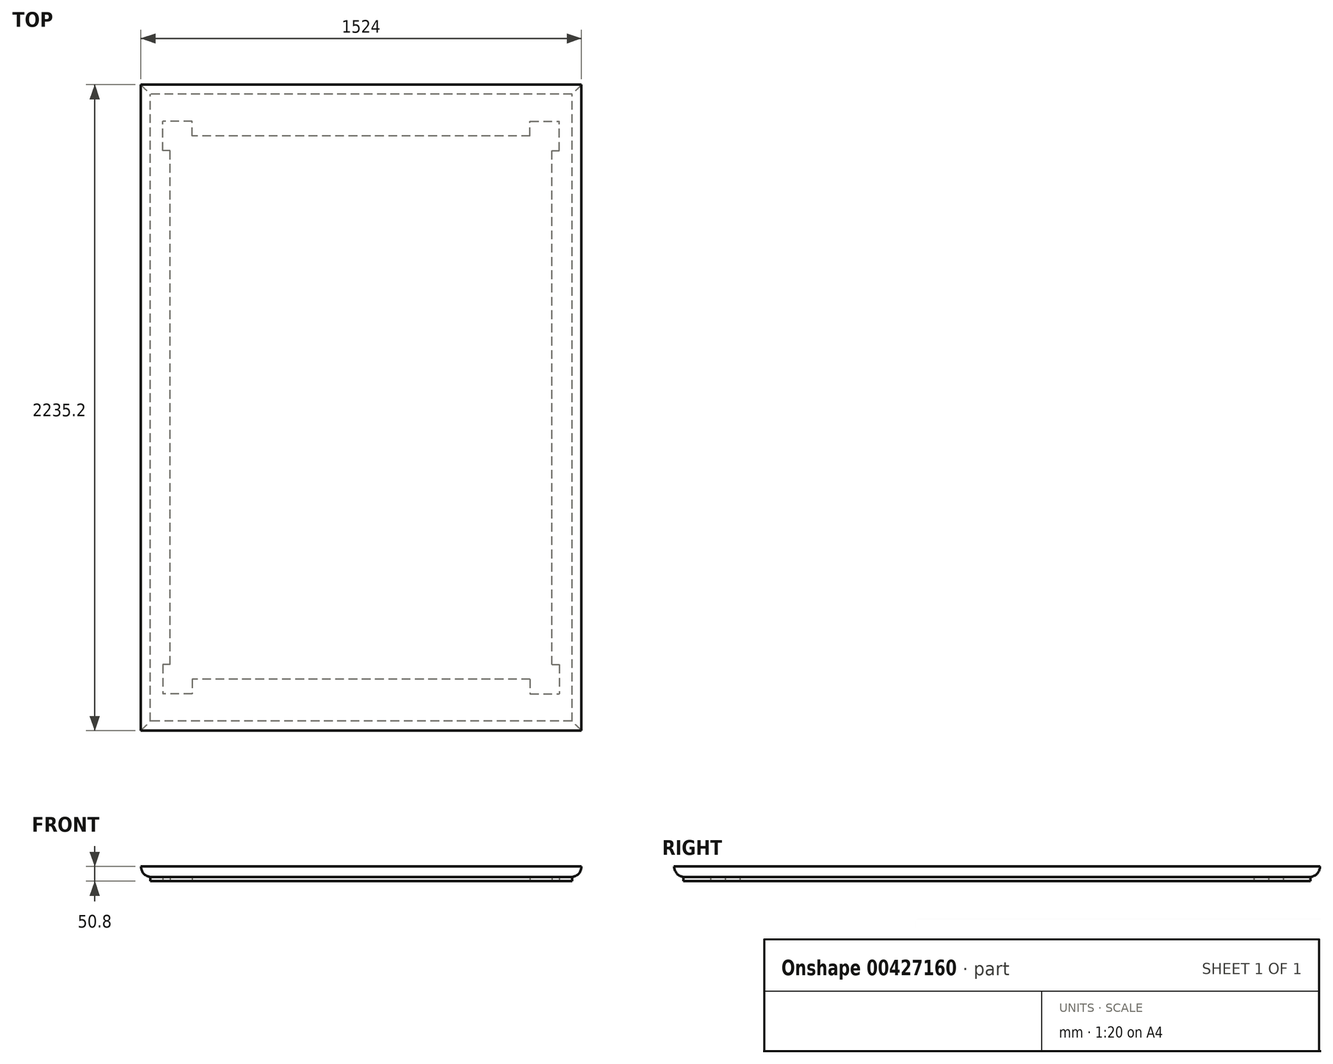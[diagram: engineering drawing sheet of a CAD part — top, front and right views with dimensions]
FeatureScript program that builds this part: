
annotation { "Feature Type Name" : "Feature", "Feature Type Description" : "" }
export const myFeature = defineFeature(function(context is Context, id is Id, definition is map)
    precondition{}
    {
        {
            var Q0;
            Q0=qCreatedBy(makeId("Top.planeOp"),FACE);
            var sketch = newSketch(context, id + "F0", { "sketchPlane" : qUnion([Q0])});
            skLineSegment(sketch, "E0.bottom", {"start": v(-762, 1117.6) * mm, "end": v(762, 1117.6) * mm});
            skLineSegment(sketch, "E0.top", {"start": v(-762, -1117.6) * mm, "end": v(762, -1117.6) * mm});
            skLineSegment(sketch, "E0.left", {"start": v(-762, 1117.6) * mm, "end": v(-762, -1117.6) * mm});
            skLineSegment(sketch, "E0.right", {"start": v(762, 1117.6) * mm, "end": v(762, -1117.6) * mm});
            skPoint(sketch, "E0.middle", {"position": v(0, 0) * mm});
            skSolve(sketch);
        }
        {
            var Q0;
            Q0=makeQuery(id+"F0.imprint","IMPRINT",FACE,{"disambiguationData":[TD([[makeQuery(id+"F0.imprint","IMPRINT",EDGE,{"derivedFrom":sQuery(id+"F0.wireOp",EDGE,"E0.bottom")}),-1.0]])]});
            extrude(context, id + "F1", {"entities" : qUnion([Q0]), "depth" : 50.8 * mm});
        }
        {
            var Q0;
            Q0=makeQuery(id+"F1.opExtrude","CAP_FACE",FACE,{"disambiguationData":[OSD([sQuery(id+"F0.wireOp",EDGE,"E0.bottom"),sQuery(id+"F0.wireOp",EDGE,"E0.top"),sQuery(id+"F0.wireOp",EDGE,"E0.left"),sQuery(id+"F0.wireOp",EDGE,"E0.right")])],"isStart":true});
            var sketch = newSketch(context, id + "F2", { "sketchPlane" : qUnion([Q0])});
            skLineSegment(sketch, "E1.bottom", {"start": v(660.4, 939.8) * mm, "end": v(-660.4, 939.8) * mm});
            skLineSegment(sketch, "E1.top", {"start": v(660.4, -939.8) * mm, "end": v(-660.4, -939.8) * mm});
            skLineSegment(sketch, "E1.left", {"start": v(660.4, 939.8) * mm, "end": v(660.4, -939.8) * mm});
            skLineSegment(sketch, "E1.right", {"start": v(-660.4, 939.8) * mm, "end": v(-660.4, -939.8) * mm});
            skPoint(sketch, "E1.middle", {"position": v(0, 0) * mm});
            skPoint(sketch, "E2.middle", {"position": v(-660.4, 939.8) * mm});
            skPoint(sketch, "E3.middle", {"position": v(660.4, 939.8) * mm});
            skPoint(sketch, "E4.middle", {"position": v(-660.4, -939.8) * mm});
            skPoint(sketch, "E5.middle", {"position": v(660.4, -939.8) * mm});
            skLineSegment(sketch, "E6.bottom", {"start": v(-584.2, 889) * mm, "end": v(-685.8, 889) * mm});
            skLineSegment(sketch, "E6.top", {"start": v(-584.2, 990.6) * mm, "end": v(-685.8, 990.6) * mm});
            skLineSegment(sketch, "E6.left", {"start": v(-584.2, 889) * mm, "end": v(-584.2, 990.6) * mm});
            skLineSegment(sketch, "E6.right", {"start": v(-685.8, 889) * mm, "end": v(-685.8, 990.6) * mm});
            skPoint(sketch, "E6.middle", {"position": v(-635, 939.8) * mm});
            skLineSegment(sketch, "E7.MirrorCS", {"start": v(584.2, 889) * mm, "end": v(584.2, 990.6) * mm});
            skLineSegment(sketch, "E8.MirrorCS", {"start": v(584.2, 889) * mm, "end": v(685.8, 889) * mm});
            skLineSegment(sketch, "E9.MirrorCS", {"start": v(584.2, 990.6) * mm, "end": v(685.8, 990.6) * mm});
            skLineSegment(sketch, "E10.MirrorCS", {"start": v(685.8, 889) * mm, "end": v(685.8, 990.6) * mm});
            skLineSegment(sketch, "E11.MirrorCS", {"start": v(-584.2, -889) * mm, "end": v(-685.8, -889) * mm});
            skLineSegment(sketch, "E12.MirrorCS", {"start": v(-584.2, -889) * mm, "end": v(-584.2, -990.6) * mm});
            skLineSegment(sketch, "E13.MirrorCS", {"start": v(-584.2, -990.6) * mm, "end": v(-685.8, -990.6) * mm});
            skLineSegment(sketch, "E14.MirrorCS", {"start": v(-685.8, -889) * mm, "end": v(-685.8, -990.6) * mm});
            skLineSegment(sketch, "E15.MirrorCS", {"start": v(584.2, -889) * mm, "end": v(685.8, -889) * mm});
            skLineSegment(sketch, "E16.MirrorCS", {"start": v(584.2, -990.6) * mm, "end": v(685.8, -990.6) * mm});
            skLineSegment(sketch, "E17.MirrorCS", {"start": v(584.2, -889) * mm, "end": v(584.2, -990.6) * mm});
            skLineSegment(sketch, "E18.MirrorCS", {"start": v(685.8, -889) * mm, "end": v(685.8, -990.6) * mm});
            skSolve(sketch);
        }
        {
            var Q0;
            Q0 = qSketchRegion(id + "F2", true);
            extrude(context, id + "F3", {"entities" : qUnion([Q0]), "operationType" : NewBodyOperationType.REMOVE, "oppositeDirection" : true, "depth" : 12.7 * mm});
        }
        {
            var Q0;
            Q0=makeQuery(id+"F1.opExtrude","SWEPT_FACE",FACE,{"disambiguationData":[OSD([sQuery(id+"F0.wireOp",EDGE,"E0.bottom")])]});
            var sketch = newSketch(context, id + "F4", { "sketchPlane" : qUnion([Q0])});
            skFitSpline(sketch, "E19", {"points": [v(-762, 50.8) * mm, v(-752.65, 26.05) * mm, v(-729.4, 13.96) * mm], "startDerivative": vector(11.64, -55.69) * mm, "endDerivative": vector(53.6, -17.97) * mm});
            skLineSegment(sketch, "E20", {"start": v(-729.4, 13.96) * mm, "end": v(-729.4, 0) * mm});
            skFitSpline(sketch, "E21.MirrorCS", {"points": [v(762, 50.8) * mm, v(752.65, 26.05) * mm, v(729.4, 13.96) * mm], "startDerivative": vector(-11.64, -55.69) * mm, "endDerivative": vector(-53.6, -17.97) * mm});
            skLineSegment(sketch, "E22.MirrorCS", {"start": v(729.4, 13.96) * mm, "end": v(729.4, 0) * mm});
            skSolve(sketch);
        }
        {
            var Q0;
            Q0=makeQuery(id+"F1.opExtrude","SWEPT_FACE",FACE,{"disambiguationData":[OSD([sQuery(id+"F0.wireOp",EDGE,"E0.left")])]});
            var sketch = newSketch(context, id + "F5", { "sketchPlane" : qUnion([Q0])});
            skFitSpline(sketch, "E23.MirrorCS", {"points": [v(1117.6, 50.8) * mm, v(1107.93, 26.33) * mm, v(1084.67, 13.96) * mm], "startDerivative": vector(-11.64, -55.69) * mm, "endDerivative": vector(-53.6, -17.97) * mm});
            skLineSegment(sketch, "E24.MirrorCS", {"start": v(1084.67, 13.96) * mm, "end": v(1084.67, 0) * mm});
            skLineSegment(sketch, "E25.MirrorCS", {"start": v(-1084.67, 13.96) * mm, "end": v(-1084.67, 0) * mm});
            skFitSpline(sketch, "E26.MirrorCS", {"points": [v(-1117.6, 50.8) * mm, v(-1107.93, 26.33) * mm, v(-1084.67, 13.96) * mm], "startDerivative": vector(11.64, -55.69) * mm, "endDerivative": vector(53.6, -17.97) * mm});
            skSolve(sketch);
        }
        {
            var Q0;
            {var subQ0=sQuery(id+"F5.wireOp",EDGE,"E25.MirrorCS");Q0=makeQuery(id+"F5.imprint","IMPRINT",FACE,{"disambiguationData":[TD([[makeQuery(id+"F5.imprint","IMPRINT",EDGE,{"derivedFrom":subQ0}),-1.0]])]});}
            var Q1;
            Q1=makeQuery(id+"F5.imprint","IMPRINT",FACE,{"disambiguationData":[TD([[makeQuery(id+"F5.imprint","IMPRINT",EDGE,{"derivedFrom":sQuery(id+"F5.wireOp",EDGE,"E23.MirrorCS")}),1.0]])]});
            extrude(context, id + "F6", {"entities" : qUnion([Q0, Q1]), "operationType" : NewBodyOperationType.REMOVE, "endBound" : BoundingType.THROUGH_ALL, "oppositeDirection" : true, "depth" : 25.4 * mm});
        }
        {
            var Q0;
            Q0=makeQuery(id+"F4.imprint","IMPRINT",FACE,{"disambiguationData":[TD([[makeQuery(id+"F4.imprint","IMPRINT",EDGE,{"derivedFrom":sQuery(id+"F4.wireOp",EDGE,"E21.MirrorCS")}),1.0]])]});
            var Q1;
            Q1=makeQuery(id+"F4.imprint","IMPRINT",FACE,{"disambiguationData":[TD([[makeQuery(id+"F4.imprint","IMPRINT",EDGE,{"derivedFrom":sQuery(id+"F4.wireOp",EDGE,"E19")}),-1.0]])]});
            extrude(context, id + "F7", {"entities" : qUnion([Q0, Q1]), "operationType" : NewBodyOperationType.REMOVE, "endBound" : BoundingType.THROUGH_ALL, "oppositeDirection" : true, "depth" : 25.4 * mm});
        }
    });
